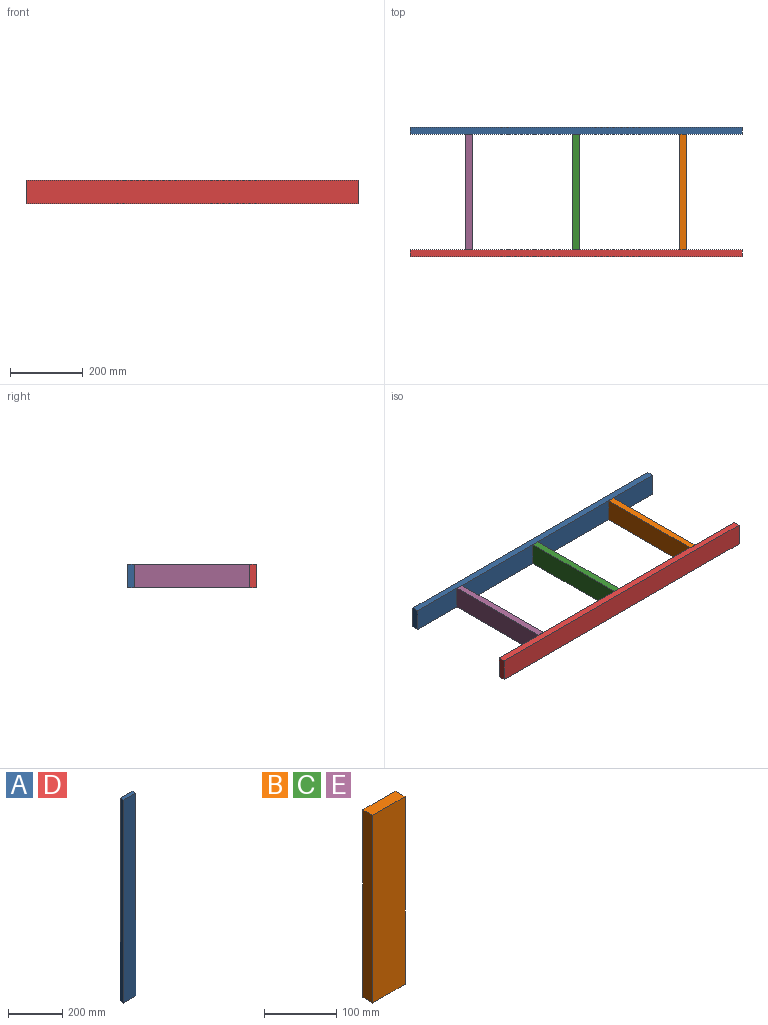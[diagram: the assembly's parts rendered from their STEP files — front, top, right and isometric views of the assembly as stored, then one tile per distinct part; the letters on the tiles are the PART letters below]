
ASSEMBLY  parts=5 mates=4
PART A: 6 faces, bbox 63.5x19.1x914.4 mm
  f0: plane 914.4x19.05mm, normal (1,0,0), area 17419.3mm2, adj f1,f3,f4,f5
  f1: plane 914.4x63.5mm, normal (0,1,0), area 58064.4mm2, adj f0,f2,f4,f5
  f2: plane 914.4x19.05mm, normal (-1,0,0), area 17419.3mm2, adj f1,f3,f4,f5
  f3: plane 914.4x63.5mm, normal (0,-1,0), area 58064.4mm2, adj f0,f2,f4,f5
  f4: plane 63.5x19.05mm, normal (0,0,1), area 1209.7mm2, adj f0,f1,f2,f3
  f5: plane 63.5x19.05mm, normal (0,0,-1), area 1209.7mm2, adj f0,f1,f2,f3
PART B: 6 faces, bbox 63.5x19.1x317.5 mm
  f0: plane 317.5x19.05mm, normal (1,0,0), area 6048.4mm2, adj f1,f3,f4,f5
  f1: plane 317.5x63.5mm, normal (0,1,0), area 20161.3mm2, adj f0,f2,f4,f5
  f2: plane 317.5x19.05mm, normal (-1,0,0), area 6048.4mm2, adj f1,f3,f4,f5
  f3: plane 317.5x63.5mm, normal (0,-1,0), area 20161.3mm2, adj f0,f2,f4,f5
  f4: plane 63.5x19.05mm, normal (0,0,1), area 1209.7mm2, adj f0,f1,f2,f3
  f5: plane 63.5x19.05mm, normal (0,0,-1), area 1209.7mm2, adj f0,f1,f2,f3
PART C: same geometry as B
PART D: same geometry as A
PART E: same geometry as B
PLACE A rot(axis=(-0.71,0,0.71),180deg) t=(457.2,168.28,0)mm
PLACE B rot(axis=(0.58,0.58,-0.58),120deg) t=(295.28,0,0)mm
PLACE C rot(axis=(0.58,-0.58,0.58),120deg) t=(0,0,0)mm
PLACE D rot(axis=(0,-1,0),90deg) t=(457.2,-168.28,0)mm
PLACE E rot(axis=(-0.58,0.58,0.58),120deg) t=(-295.27,0,0)mm
MATE fastened A.f1 <-> C.f5  axis (0,-1,0) through (0,158.75,0)mm
MATE fastened E.f4 <-> A.f1  axis (0,1,0) through (-295.27,158.75,0)mm
MATE fastened D.f1 <-> C.f4  axis (0,1,0) through (0,-158.75,0)mm
MATE fastened B.f4 <-> D.f1  axis (0,-1,0) through (295.28,-158.75,0)mm
